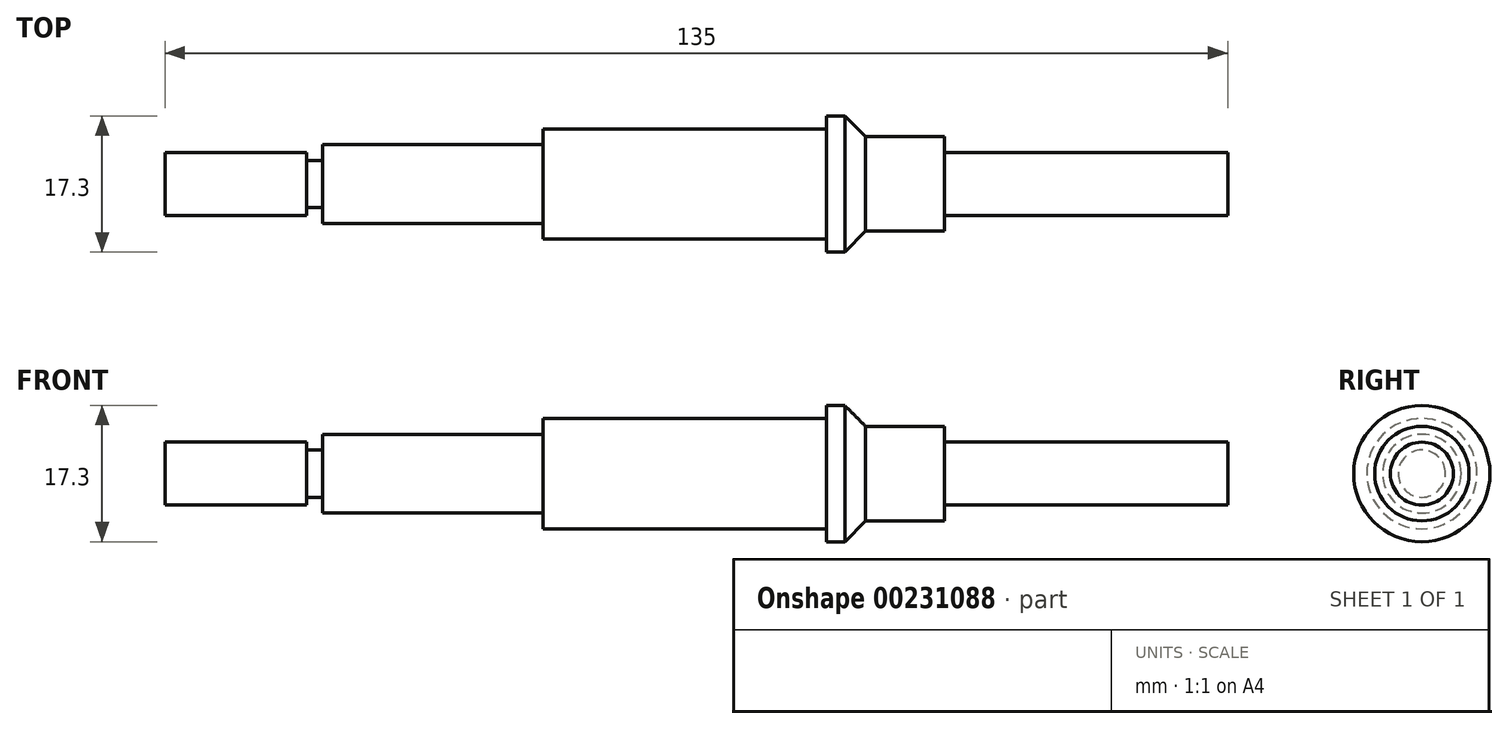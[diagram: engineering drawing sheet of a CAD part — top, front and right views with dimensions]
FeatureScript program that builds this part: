
annotation { "Feature Type Name" : "Feature", "Feature Type Description" : "" }
export const myFeature = defineFeature(function(context is Context, id is Id, definition is map)
    precondition{}
    {
        {
            var Q0;
            Q0=qCreatedBy(makeId("Front.planeOp"),FACE);
            var sketch = newSketch(context, id + "F0", { "sketchPlane" : qUnion([Q0])});
            skLineSegment(sketch, "E0", {"start": v(73.18, -4.07) * mm, "end": v(73.18, -0.07) * mm});
            skLineSegment(sketch, "E1", {"start": v(73.18, -0.07) * mm, "end": v(37.18, -0.07) * mm});
            skLineSegment(sketch, "E2", {"start": v(37.18, -0.07) * mm, "end": v(37.18, 1.93) * mm});
            skLineSegment(sketch, "E3", {"start": v(37.18, 1.93) * mm, "end": v(27.18, 1.93) * mm});
            skLineSegment(sketch, "E4", {"start": v(22.18, 4.58) * mm, "end": v(22.18, 2.93) * mm});
            skLineSegment(sketch, "E5", {"start": v(22.18, 2.93) * mm, "end": v(-13.82, 2.93) * mm});
            skLineSegment(sketch, "E6", {"start": v(-13.82, 2.93) * mm, "end": v(-13.82, 0.93) * mm});
            skLineSegment(sketch, "E7", {"start": v(-13.82, 0.93) * mm, "end": v(-41.82, 0.93) * mm});
            skLineSegment(sketch, "E8", {"start": v(-61.82, -4.07) * mm, "end": v(-61.82, -0.07) * mm});
            skLineSegment(sketch, "E9", {"start": v(-61.82, -0.07) * mm, "end": v(-43.82, -0.07) * mm});
            skLineSegment(sketch, "E10", {"start": v(-43.82, -0.07) * mm, "end": v(-43.82, -1.07) * mm});
            skLineSegment(sketch, "E11", {"start": v(-43.82, -1.07) * mm, "end": v(-41.82, -1.07) * mm});
            skLineSegment(sketch, "E12", {"start": v(-41.82, -1.07) * mm, "end": v(-41.82, 0.93) * mm});
            skLineSegment(sketch, "E13", {"start": v(22.18, 4.58) * mm, "end": v(24.53, 4.58) * mm});
            skLineSegment(sketch, "E14", {"start": v(24.53, 4.58) * mm, "end": v(27.18, 1.93) * mm});
            skLineSegment(sketch, "E15", {"start": v(-61.82, -4.07) * mm, "end": v(73.18, -4.07) * mm});
            skSolve(sketch);
        }
        {
            var Q0;
            Q0 = qSketchRegion(id + "F0", true);
            var Q1;
            Q1=sQuery(id+"F0.wireOp",EDGE,"E0");
            var Q2;
            Q2=sQuery(id+"F0.wireOp",EDGE,"E1");
            var Q3;
            Q3=sQuery(id+"F0.wireOp",EDGE,"E2");
            var Q4;
            Q4=sQuery(id+"F0.wireOp",EDGE,"E3");
            var Q5;
            Q5=sQuery(id+"F0.wireOp",EDGE,"E4");
            var Q6;
            Q6=sQuery(id+"F0.wireOp",EDGE,"E5");
            var Q7;
            Q7=sQuery(id+"F0.wireOp",EDGE,"E6");
            var Q8;
            Q8=sQuery(id+"F0.wireOp",EDGE,"E7");
            var Q9;
            Q9=sQuery(id+"F0.wireOp",EDGE,"E8");
            var Q10;
            Q10=sQuery(id+"F0.wireOp",EDGE,"E9");
            var Q11;
            Q11=sQuery(id+"F0.wireOp",EDGE,"E10");
            var Q12;
            Q12=sQuery(id+"F0.wireOp",EDGE,"E11");
            var Q13;
            Q13=sQuery(id+"F0.wireOp",EDGE,"E12");
            var Q14;
            Q14=sQuery(id+"F0.wireOp",EDGE,"E13");
            var Q15;
            Q15=sQuery(id+"F0.wireOp",EDGE,"E14");
            var Q16;
            Q16=sQuery(id+"F0.wireOp",EDGE,"E15");
            var Q17;
            Q17=sQuery(id+"F0.wireOp",EDGE,"E15");
            revolve(context, id + "F1", {"entities" : qUnion([Q0]), "surfaceEntities" : qUnion([Q1, Q2, Q3, Q4, Q5, Q6, Q7, Q8, Q9, Q10, Q11, Q12, Q13, Q14, Q15, Q16]), "axis" : qUnion([Q17]), "revolveType" : RevolveType.FULL});
        }
    });
